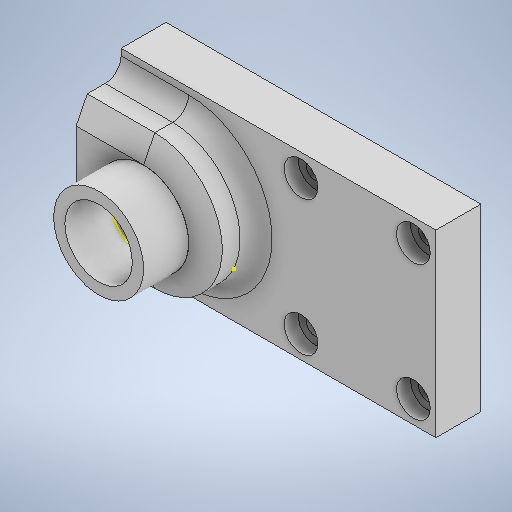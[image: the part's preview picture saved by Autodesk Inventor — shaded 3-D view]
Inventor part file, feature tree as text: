
AUTODESK INVENTOR PART (.ipt)
format: ipt  version: 2025.2 (Build 292293000, 293)  size: 420,352 bytes
history: native  units: in
note: dims shown in document units (in); Inventor stores cm internally (conversion verified against a paired STEP export)
features: sketch x6, extrude x5, fillet x1, chamfer x1, other x1
ambient origin geometry x8: Origin, YZ Plane, XZ Plane, XY Plane, X Axis, Y Axis, Z Axis, Center Point
bodies: Solid1 (feature_tree)
feature tree (14):
  extrude  "Extrusion1"  Depth=2.0in
  extrude  "Extrusion2"  Depth=0.25in
  extrude  "Extrusion3"  Depth=0.25in
  fillet  "Face Fillet1"
  extrude  "Extrusion4"  Depth=0.5in
  extrude  "Extrusion5"  Depth=0.3752in
  chamfer  "Chamfer1"  Distance=0.1575in
  sketch  "Sketch6"  dims[d22=0.3752in d23=0.1575in d24=0.0in d25=0.75in d26=0.75in d29=0.75in d30=0.5in d31=0.0in d32=0.1772in d36=0.5in d37=0.0in d38=1.0in d39=0.75in d40=0.5in d41=0.0in d42=0.248in d43=0.1181in d44=0.1828in]
  sketch  "Sketch1"  dims[d5=3.5in d6=2.0in]
  other  "Image1"
  sketch  "Sketch2"  dims[d7=0.2012in d8=0.25in]
  sketch  "Sketch3"  dims[d9=0.25in d11=0.2012in]
  sketch  "Sketch4"  dims[d17=0.5in d18=0.0in d19=0.3752in]
  sketch  "Sketch5"  dims[d20=0.3752in d21=0.3752in]
